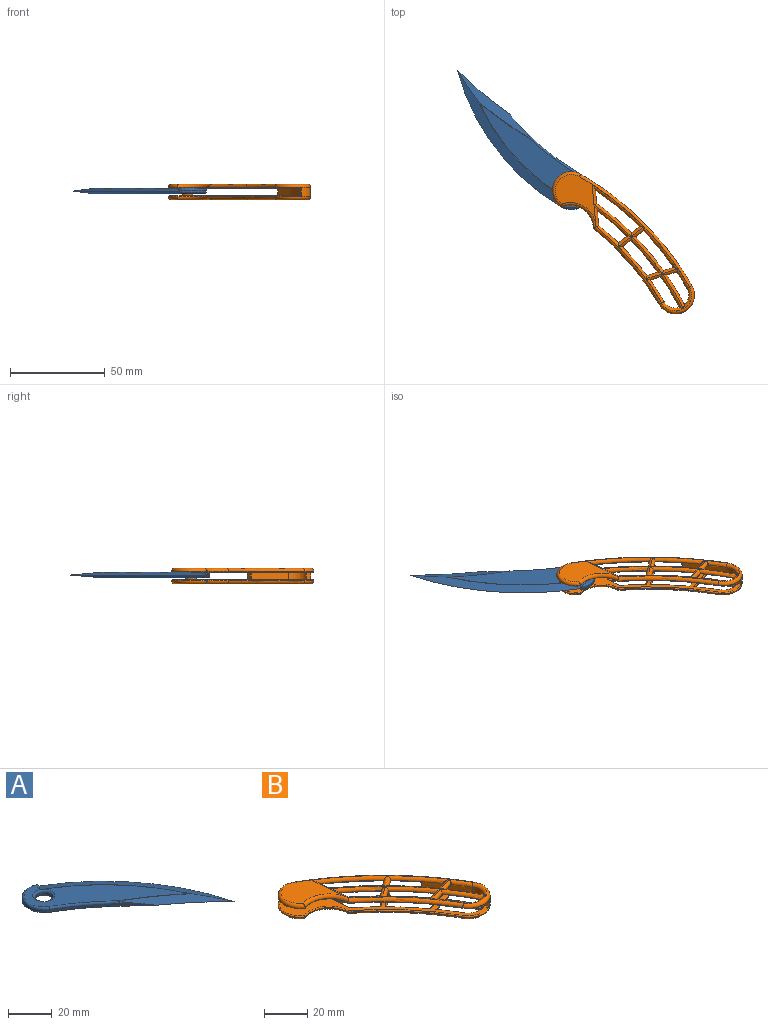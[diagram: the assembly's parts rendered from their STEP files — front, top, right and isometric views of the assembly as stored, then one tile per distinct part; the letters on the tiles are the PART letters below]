
ASSEMBLY  parts=2 mates=1
PART A: 25 faces, bbox 74.4x78.3x3 mm
  f0: cylinder r=140.99mm len=37.78mm, axis (0,0,-1), area 47.3mm2, adj f3,f5,f9,f14,f17
  f1: plane 57.18x54.85mm, normal (0,0,1), area 711.1mm2, adj f15,f17,f19,f20,f21,f24
  f2: plane 57.58x55.37mm, normal (0,0,-1), area 725.8mm2, adj f3,f4,f10,f13,f14,f23
  f3: cone r=205mm half-angle=73.3deg, axis (0,0,-1), area 186.3mm2, adj f0,f2,f4,f5,f14
  f4: cone r=117.87mm half-angle=73.3deg, axis (0,0,1), area 427mm2, adj f2,f3,f6,f8,f9,f10,f11
  f5: cone r=200mm half-angle=73.3deg, axis (0,0,1), area 181.4mm2, adj f0,f3,f6,f17,f19
  f6: cone r=112.87mm half-angle=73.3deg, axis (0,0,-1), area 416.8mm2, adj f4,f5,f7,f9,f16,f20,f21
  f7: plane 0.57x0.33mm, normal (0.87,-0.5,0), area 0.1mm2, adj f6,f16,f20
  f8: plane 0.57x0.33mm, normal (0.87,-0.5,0), area 0.1mm2, adj f4,f10,f11
  f9: cylinder r=10mm len=18.65mm, axis (0,0,-1), area 30.9mm2, adj f0,f4,f6,f11,f13,f15,f16
  f10: cylinder r=0.99mm len=3.92mm, axis (-0.5,-0.87,0), area 4.3mm2, adj f2,f4,f8,f12
  f11: cylinder r=0.99mm len=1.4mm, axis (0,0,-1), area 0.6mm2, adj f4,f8,f9,f12
  f12: sphere r=0.99mm, area 1.6mm2, adj f10,f11,f13
  f13: torus R=9.01mm, axis (0,0,1), area 45.4mm2, adj f2,f9,f12,f14
  f14: torus R=141.98mm, axis (0,0,1), area 55.3mm2, adj f0,f2,f3,f13
  f15: torus R=9.01mm, axis (0,0,1), area 45.4mm2, adj f1,f9,f17,f18
  f16: cylinder r=0.99mm len=1.4mm, axis (0,0,-1), area 0.6mm2, adj f6,f7,f9,f18
  f17: torus R=141.98mm, axis (0,0,1), area 55.4mm2, adj f0,f1,f5,f15,f19
  f18: sphere r=0.99mm, area 1.6mm2, adj f15,f16,f20
  f19: torus R=205.15mm, axis (0,0,1), area 9.6mm2, adj f1,f5,f17,f21
  f20: cylinder r=0.99mm len=4.02mm, axis (0.5,0.87,0), area 4.3mm2, adj f1,f6,f7,f18,f21,f24
  f21: torus R=112.72mm, axis (0,0,1), area 20.2mm2, adj f1,f6,f19,f20,f24
  f22: cylinder r=4mm len=8mm, axis (0,0,1), area 25.1mm2, adj f23,f24
  f23: torus R=5mm, axis (0,0,1), area 43.1mm2, adj f2,f22
  f24: torus R=5mm, axis (0,0,1), area 42.9mm2, adj f1,f20,f21,f22
PART B: 214 faces, bbox 86x86x8.2 mm
  f0: plane 72.02x72.02mm, normal (0,0,1), area 286.6mm2, adj f86,f87,f88,f89,f92,f93,f94,f95
  f1: plane 72.02x72.02mm, normal (0,0,-1), area 286.6mm2, adj f58,f59,f60,f61,f63,f64,f66,f67
  f2: plane 74x68.82mm, normal (0,0,1), area 756mm2, adj f143,f149,f152,f153,f156,f157,f160,f161
  f3: plane 74x68.82mm, normal (0,0,-1), area 756mm2, adj f124,f128,f129,f131,f133,f134,f140,f141
  f4: cylinder r=140.99mm len=40.13mm, axis (0,0,-1), area 0.5mm2, adj f6,f8,f115,f166
  f5: cylinder r=10mm len=18.65mm, axis (0,0,-1), area 0.3mm2, adj f6,f9,f118,f156
  f6: cylinder r=12mm len=16.55mm, axis (0,0,-1), area 0.2mm2, adj f4,f5,f117,f160
  f7: cylinder r=140.99mm len=40.13mm, axis (0,0,-1), area 0.5mm2, adj f8,f11,f120,f155
  f8: cylinder r=10mm len=18.65mm, axis (0,0,-1), area 80mm2, adj f4,f7,f9,f114,f119,f159,f165,f168
  f9: cylinder r=160.99mm len=58.64mm, axis (0,0,-1), area 127.3mm2, adj f5,f8,f10,f116,f121,f137,f141,f142
  f10: cylinder r=10mm len=18.65mm, axis (0,0,-1), area 0.3mm2, adj f9,f11,f123,f147
  f11: cylinder r=12mm len=16.55mm, axis (0,0,-1), area 0.2mm2, adj f7,f10,f122,f151
  f12: cylinder r=157.99mm len=30.39mm, axis (0,0,1), area 116.7mm2, adj f15,f33,f54,f59,f61,f99,f104,f127
  f13: plane 3.2x1.56mm, normal (-0.63,0.78,0), area 6.4mm2, adj f134,f138,f142,f143
  f14: plane 3.2x2.15mm, normal (-0.87,-0.5,0), area 8mm2, adj f15,f158,f168,f174
  f15: cylinder r=7mm len=9.57mm, axis (0,0,1), area 53.4mm2, adj f12,f14,f64,f105,f145,f150,f154,f176
  f16: cylinder r=152.65mm len=18.35mm, axis (0,0,1), area 0.2mm2, adj f17,f19,f110,f210
  f17: plane 6.96x0.64mm, normal (1,0.09,0), area 0.1mm2, adj f16,f18,f112,f209
  f18: cylinder r=157.99mm len=23.29mm, axis (0,0,1), area 0.3mm2, adj f17,f19,f113,f211
  f19: plane 4.3x3.26mm, normal (-0.6,0.8,0), area 0.1mm2, adj f16,f18,f111,f212
  f20: cylinder r=149.65mm len=16.16mm, axis (0,0,1), area 0.2mm2, adj f21,f23,f88,f207
  f21: cylinder r=7mm len=8.18mm, axis (0,0,1), area 0.1mm2, adj f20,f22,f92,f205
  f22: cylinder r=143.99mm len=11.23mm, axis (0,0,1), area 0.1mm2, adj f21,f23,f94,f206
  f23: plane 5.67x1.77mm, normal (0.3,-0.95,0), area 0.1mm2, adj f20,f22,f91,f208
  f24: cylinder r=149.65mm len=16.86mm, axis (0,0,1), area 0.2mm2, adj f25,f27,f87,f203
  f25: plane 5.71x1.78mm, normal (-0.3,0.95,0), area 0.1mm2, adj f24,f26,f90,f201
  f26: cylinder r=143.99mm len=15.19mm, axis (0,0,1), area 0.2mm2, adj f25,f27,f93,f202
  f27: plane 4.54x3.45mm, normal (0.6,-0.8,0), area 0.1mm2, adj f24,f26,f89,f204
  f28: cylinder r=149.65mm len=15.57mm, axis (0,0,1), area 0.2mm2, adj f29,f31,f108,f199
  f29: plane 4.55x3.46mm, normal (-0.6,0.8,0), area 0.1mm2, adj f28,f30,f109,f197
  f30: cylinder r=143.99mm len=10.31mm, axis (0,0,1), area 0.1mm2, adj f29,f31,f107,f198
  f31: plane 7.7x0.71mm, normal (1,0.09,0), area 0.1mm2, adj f28,f30,f106,f200
  f32: cylinder r=152.65mm len=17.74mm, axis (0,0,1), area 0.2mm2, adj f33,f34,f97,f124
  f33: plane 4.29x3.26mm, normal (0.6,-0.8,0), area 0.1mm2, adj f12,f32,f96,f129
  f34: plane 4.71x1.47mm, normal (-0.3,0.95,0), area 0mm2, adj f32,f98,f127,f128
  f35: plane 4.97x1.55mm, normal (0.3,-0.95,0), area 0.1mm2, adj f36,f101,f132,f140
  f36: cylinder r=152.65mm len=14.98mm, axis (0,0,1), area 0.2mm2, adj f35,f103,f145,f146
  f37: plane 4.3x3.26mm, normal (-0.6,0.8,0), area 0.1mm2, adj f38,f40,f85,f196
  f38: cylinder r=157.99mm len=23.29mm, axis (0,0,1), area 0.3mm2, adj f37,f39,f84,f195
  f39: plane 6.96x0.64mm, normal (1,0.09,0), area 0.1mm2, adj f38,f40,f82,f193
  f40: cylinder r=152.65mm len=18.35mm, axis (0,0,1), area 0.2mm2, adj f37,f39,f83,f194
  f41: plane 5.67x1.77mm, normal (0.3,-0.95,0), area 0.1mm2, adj f42,f44,f74,f192
  f42: cylinder r=143.99mm len=11.23mm, axis (0,0,1), area 0.1mm2, adj f41,f43,f73,f190
  f43: cylinder r=7mm len=8.18mm, axis (0,0,1), area 0.1mm2, adj f42,f44,f72,f189
  f44: cylinder r=149.65mm len=16.16mm, axis (0,0,1), area 0.2mm2, adj f41,f43,f75,f191
  f45: plane 4.54x3.45mm, normal (0.6,-0.8,0), area 0.1mm2, adj f46,f48,f81,f188
  f46: cylinder r=143.99mm len=15.19mm, axis (0,0,1), area 0.2mm2, adj f45,f47,f79,f186
  f47: plane 5.71x1.78mm, normal (-0.3,0.95,0), area 0.1mm2, adj f46,f48,f77,f185
  f48: cylinder r=149.65mm len=16.86mm, axis (0,0,1), area 0.2mm2, adj f45,f47,f80,f187
  f49: plane 7.7x0.71mm, normal (1,0.09,0), area 0.1mm2, adj f50,f52,f71,f184
  f50: cylinder r=143.99mm len=10.31mm, axis (0,0,1), area 0.1mm2, adj f49,f51,f69,f182
  f51: plane 4.55x3.46mm, normal (-0.6,0.8,0), area 0.1mm2, adj f50,f52,f68,f181
  f52: cylinder r=149.65mm len=15.57mm, axis (0,0,1), area 0.2mm2, adj f49,f51,f70,f183
  f53: plane 4.71x1.47mm, normal (-0.3,0.95,0), area 0mm2, adj f55,f62,f161,f163
  f54: plane 4.29x3.26mm, normal (0.6,-0.8,0), area 0.1mm2, adj f12,f55,f60,f153
  f55: cylinder r=152.65mm len=17.74mm, axis (0,0,1), area 0.2mm2, adj f53,f54,f63,f157
  f56: cylinder r=152.65mm len=14.98mm, axis (0,0,1), area 0.2mm2, adj f57,f67,f177,f179
  f57: plane 4.97x1.55mm, normal (0.3,-0.95,0), area 0.1mm2, adj f56,f65,f171,f175
  f58: torus R=159.48mm, axis (0,0,1), area 0mm2, adj f1,f59,f61,f162,f164
  f59: torus R=159.48mm, axis (0,0,1), area 60.6mm2, adj f1,f12,f58,f60,f162
  f60: cylinder r=1.49mm len=7.59mm, axis (-0.8,-0.6,0), area 16.1mm2, adj f1,f54,f59,f63
  f61: torus R=159.48mm, axis (0,0,1), area 24.1mm2, adj f1,f12,f58,f64,f164
  f62: cylinder r=1.49mm len=8.62mm, axis (0.95,0.3,0), area 15.4mm2, adj f53,f63,f65,f162
  f63: torus R=151.16mm, axis (0,0,1), area 56.3mm2, adj f1,f55,f60,f62,f66
  f64: torus R=8.49mm, axis (0,0,1), area 25.1mm2, adj f1,f15,f61,f180
  f65: cylinder r=1.49mm len=8.63mm, axis (-0.95,-0.3,0), area 14.7mm2, adj f57,f62,f67,f162,f164
  f66: torus R=151.16mm, axis (0,0,1), area 0mm2, adj f1,f63,f67
  f67: torus R=151.16mm, axis (0,0,1), area 44.7mm2, adj f1,f56,f65,f66,f180
  f68: cylinder r=1.49mm len=7.84mm, axis (0.8,0.6,0), area 16.9mm2, adj f1,f51,f69,f70
  f69: torus R=142.5mm, axis (0,0,1), area 34.4mm2, adj f1,f50,f68,f71
  f70: torus R=151.14mm, axis (0,0,1), area 54.1mm2, adj f1,f52,f68,f71
  f71: cylinder r=1.49mm len=11.75mm, axis (0.09,-1,0), area 22.7mm2, adj f1,f49,f69,f70
  f72: torus R=8.49mm, axis (0,0,1), area 25.8mm2, adj f1,f43,f73,f75
  f73: torus R=142.5mm, axis (0,0,1), area 32.9mm2, adj f1,f42,f72,f74,f76
  f74: cylinder r=1.49mm len=9mm, axis (-0.95,-0.3,0), area 17mm2, adj f41,f73,f75,f77
  f75: torus R=151.14mm, axis (0,0,1), area 46.7mm2, adj f1,f44,f72,f74,f78
  f76: torus R=142.5mm, axis (0,0,1), area 0mm2, adj f1,f73,f79
  f77: cylinder r=1.49mm len=9mm, axis (0.95,0.3,0), area 17.1mm2, adj f47,f74,f79,f80
  f78: torus R=151.14mm, axis (0,0,1), area 0mm2, adj f1,f75,f80
  f79: torus R=142.5mm, axis (0,0,1), area 49mm2, adj f1,f46,f76,f77,f81
  f80: torus R=151.14mm, axis (0,0,1), area 54.7mm2, adj f1,f48,f77,f78,f81
  f81: cylinder r=1.49mm len=7.84mm, axis (-0.8,-0.6,0), area 16.9mm2, adj f1,f45,f79,f80
  f82: cylinder r=1.49mm len=10.87mm, axis (0.09,-1,0), area 20.8mm2, adj f1,f39,f83,f84
  f83: torus R=151.16mm, axis (0,0,1), area 58.4mm2, adj f1,f40,f82,f85
  f84: torus R=159.48mm, axis (0,0,1), area 76.6mm2, adj f1,f38,f82,f85
  f85: cylinder r=1.49mm len=7.59mm, axis (0.8,0.6,0), area 16.1mm2, adj f1,f37,f83,f84
  f86: torus R=151.14mm, axis (0,0,1), area 0mm2, adj f0,f87,f88
  f87: torus R=151.14mm, axis (0,0,1), area 54.7mm2, adj f0,f24,f86,f89,f90
  f88: torus R=151.14mm, axis (0,0,1), area 46.7mm2, adj f0,f20,f86,f91,f92
  f89: cylinder r=1.49mm len=7.84mm, axis (0.8,0.6,0), area 16.9mm2, adj f0,f27,f87,f93
  f90: cylinder r=1.49mm len=9mm, axis (-0.95,-0.3,0), area 17.1mm2, adj f25,f87,f91,f93
  f91: cylinder r=1.49mm len=9mm, axis (0.95,0.3,0), area 17mm2, adj f23,f88,f90,f94
  f92: torus R=8.49mm, axis (0,0,1), area 25.8mm2, adj f0,f21,f88,f94
  f93: torus R=142.5mm, axis (0,0,1), area 49mm2, adj f0,f26,f89,f90,f95
  f94: torus R=142.5mm, axis (0,0,1), area 32.9mm2, adj f0,f22,f91,f92,f95
  f95: torus R=142.5mm, axis (0,0,1), area 0mm2, adj f0,f93,f94
  f96: cylinder r=1.49mm len=7.59mm, axis (0.8,0.6,0), area 16.1mm2, adj f0,f33,f97,f99
  f97: torus R=151.16mm, axis (0,0,1), area 56.3mm2, adj f0,f32,f96,f98,f100
  f98: cylinder r=1.49mm len=8.62mm, axis (-0.95,-0.3,0), area 15.4mm2, adj f34,f97,f101,f125
  f99: torus R=159.48mm, axis (0,0,1), area 60.6mm2, adj f0,f12,f96,f102,f125
  f100: torus R=151.16mm, axis (0,0,1), area 0mm2, adj f0,f97,f103
  f101: cylinder r=1.49mm len=8.63mm, axis (0.95,0.3,0), area 14.7mm2, adj f35,f98,f103,f125,f126
  f102: torus R=159.48mm, axis (0,0,1), area 0mm2, adj f0,f99,f104,f125,f126
  f103: torus R=151.16mm, axis (0,0,1), area 44.7mm2, adj f0,f36,f100,f101,f139
  f104: torus R=159.48mm, axis (0,0,1), area 24.1mm2, adj f0,f12,f102,f105,f126
  f105: torus R=8.49mm, axis (0,0,1), area 25.1mm2, adj f0,f15,f104,f139
  f106: cylinder r=1.49mm len=11.75mm, axis (-0.09,1,0), area 22.7mm2, adj f0,f31,f107,f108
  f107: torus R=142.5mm, axis (0,0,1), area 34.4mm2, adj f0,f30,f106,f109
  f108: torus R=151.14mm, axis (0,0,1), area 54.1mm2, adj f0,f28,f106,f109
  f109: cylinder r=1.49mm len=7.84mm, axis (-0.8,-0.6,0), area 16.9mm2, adj f0,f29,f107,f108
  f110: torus R=151.16mm, axis (0,0,1), area 58.4mm2, adj f0,f16,f111,f112
  f111: cylinder r=1.49mm len=7.59mm, axis (-0.8,-0.6,0), area 16.1mm2, adj f0,f19,f110,f113
  f112: cylinder r=1.49mm len=10.87mm, axis (-0.09,1,0), area 20.8mm2, adj f0,f17,f110,f113
  f113: torus R=159.48mm, axis (0,0,1), area 76.6mm2, adj f0,f18,f111,f112
  f114: torus R=8.51mm, axis (0,0,1), area 69.5mm2, adj f1,f8,f115,f116
  f115: torus R=142.48mm, axis (0,0,1), area 124.7mm2, adj f1,f4,f114,f117
  f116: torus R=159.5mm, axis (0,0,1), area 195.7mm2, adj f1,f9,f114,f118
  f117: torus R=13.49mm, axis (0,0,1), area 56.1mm2, adj f1,f6,f115,f118
  f118: torus R=8.51mm, axis (0,0,1), area 68.7mm2, adj f1,f5,f116,f117
  f119: torus R=8.51mm, axis (0,0,1), area 69.5mm2, adj f0,f8,f120,f121
  f120: torus R=142.48mm, axis (0,0,1), area 124.7mm2, adj f0,f7,f119,f122
  f121: torus R=159.5mm, axis (0,0,1), area 195.7mm2, adj f0,f9,f119,f123
  f122: torus R=13.49mm, axis (0,0,1), area 56.1mm2, adj f0,f11,f120,f123
  f123: torus R=8.51mm, axis (0,0,1), area 68.7mm2, adj f0,f10,f121,f122
  f124: torus R=152.15mm, axis (0,0,1), area 18.5mm2, adj f3,f32,f128,f129
  f125: bspline ~2.99x1.63mm, area 1.7mm2, adj f98,f99,f101,f102,f126,f127
  f126: bspline ~2.04x1.67mm, area 1mm2, adj f101,f102,f104,f125,f132
  f127: cylinder r=0.5mm len=0.76mm, axis (0,0,1), area 0mm2, adj f12,f34,f125,f130
  f128: cylinder r=0.5mm len=5.51mm, axis (0.95,0.3,0), area 4.1mm2, adj f3,f34,f124,f130
  f129: cylinder r=0.5mm len=5.39mm, axis (-0.8,-0.6,0), area 4.6mm2, adj f3,f33,f124,f131
  f130: bspline ~1.24x1.21mm, area 1mm2, adj f12,f127,f128,f133
  f131: torus R=158.49mm, axis (0,0,1), area 10.8mm2, adj f3,f12,f129,f135
  f132: cylinder r=0.5mm len=0.57mm, axis (0,0,1), area 0mm2, adj f12,f35,f126,f136
  f133: torus R=157.49mm, axis (0,0,1), area 1.5mm2, adj f3,f12,f130,f136
  f134: cylinder r=0.5mm len=1.87mm, axis (-0.78,-0.63,0), area 1.6mm2, adj f3,f13,f135,f137
  f135: bspline ~1.18x1.17mm, area 0.8mm2, adj f12,f131,f134,f138
  f136: bspline ~1.22x1.06mm, area 0.8mm2, adj f12,f132,f133,f140
  f137: bspline ~1.22x1.07mm, area 0.8mm2, adj f9,f134,f141,f142
  f138: cylinder r=0.5mm len=3.2mm, axis (0,0,1), area 2.5mm2, adj f12,f13,f135,f144
  f139: bspline ~2.83x1.64mm, area 1.1mm2, adj f103,f105,f145
  f140: cylinder r=0.5mm len=5.77mm, axis (-0.95,-0.3,0), area 4.2mm2, adj f3,f35,f136,f146
  f141: torus R=160.49mm, axis (0,0,1), area 46.1mm2, adj f3,f9,f137,f147
  f142: cylinder r=0.5mm len=3.2mm, axis (0,0,-1), area 2.5mm2, adj f9,f13,f137,f148
  f143: cylinder r=0.5mm len=1.87mm, axis (0.78,0.63,0), area 1.6mm2, adj f2,f13,f144,f148
  f144: bspline ~1.22x1.16mm, area 0.8mm2, adj f12,f138,f143,f149
  f145: cylinder r=0.5mm len=0.82mm, axis (0,0,1), area 0mm2, adj f15,f36,f139,f150
  f146: torus R=152.15mm, axis (0,0,1), area 14.1mm2, adj f3,f36,f140,f150
  f147: torus R=9.5mm, axis (0,0,1), area 24.1mm2, adj f3,f10,f141,f151
  f148: bspline ~1.17x1.09mm, area 0.8mm2, adj f9,f142,f143,f152
  f149: torus R=158.49mm, axis (0,0,1), area 10.8mm2, adj f2,f12,f144,f153
  f150: bspline ~1.21x1.19mm, area 1mm2, adj f15,f145,f146,f154
  f151: torus R=12.5mm, axis (0,0,1), area 18.7mm2, adj f3,f11,f147,f155
  f152: torus R=160.49mm, axis (0,0,1), area 46.1mm2, adj f2,f9,f148,f156
  f153: cylinder r=0.5mm len=5.39mm, axis (0.8,0.6,0), area 4.6mm2, adj f2,f54,f149,f157
  f154: torus R=6.5mm, axis (0,0,1), area 1mm2, adj f3,f15,f150,f158
  f155: torus R=141.49mm, axis (0,0,1), area 41.9mm2, adj f3,f7,f151,f159
  f156: torus R=9.5mm, axis (0,0,1), area 24.1mm2, adj f2,f5,f152,f160
  f157: torus R=152.15mm, axis (0,0,1), area 18.5mm2, adj f2,f55,f153,f161
  f158: cylinder r=0.5mm len=2.85mm, axis (0.5,-0.87,0), area 2.2mm2, adj f3,f14,f154,f165
  f159: torus R=9.5mm, axis (0,0,1), area 11.7mm2, adj f3,f8,f155,f165
  f160: torus R=12.5mm, axis (0,0,1), area 18.7mm2, adj f2,f6,f156,f166
  f161: cylinder r=0.5mm len=5.51mm, axis (-0.95,-0.3,0), area 4.1mm2, adj f2,f53,f157,f167
  f162: bspline ~2.99x1.63mm, area 1.7mm2, adj f58,f59,f62,f65,f163,f164
  f163: cylinder r=0.5mm len=0.76mm, axis (0,0,1), area 0mm2, adj f12,f53,f162,f167
  f164: bspline ~2.04x1.67mm, area 1mm2, adj f58,f61,f65,f162,f171
  f165: bspline ~1.24x1.17mm, area 0.9mm2, adj f8,f158,f159,f168
  f166: torus R=141.49mm, axis (0,0,1), area 41.9mm2, adj f2,f4,f160,f169
  f167: bspline ~1.21x1.2mm, area 1mm2, adj f12,f161,f163,f170
  f168: cylinder r=0.5mm len=3.2mm, axis (0,0,-1), area 2.6mm2, adj f8,f14,f165,f172
  f169: torus R=9.5mm, axis (0,0,1), area 11.7mm2, adj f2,f8,f166,f172
  f170: torus R=157.49mm, axis (0,0,1), area 1.5mm2, adj f2,f12,f167,f173
  f171: cylinder r=0.5mm len=0.57mm, axis (0,0,1), area 0mm2, adj f12,f57,f164,f173
  f172: bspline ~1.22x1.22mm, area 0.9mm2, adj f8,f168,f169,f174
  f173: bspline ~1.2x1.1mm, area 0.8mm2, adj f12,f170,f171,f175
  f174: cylinder r=0.5mm len=2.85mm, axis (-0.5,0.87,0), area 2.2mm2, adj f2,f14,f172,f176
  f175: cylinder r=0.5mm len=5.77mm, axis (0.95,0.3,0), area 4.2mm2, adj f2,f57,f173,f177
  f176: torus R=6.5mm, axis (0,0,1), area 1mm2, adj f2,f15,f174,f178
  f177: torus R=152.15mm, axis (0,0,1), area 14.1mm2, adj f2,f56,f175,f178
  f178: bspline ~1.21x1.18mm, area 1mm2, adj f15,f176,f177,f179
  f179: cylinder r=0.5mm len=0.82mm, axis (0,0,1), area 0mm2, adj f15,f56,f178,f180
  f180: bspline ~2.83x1.64mm, area 1.1mm2, adj f64,f67,f179
  f181: cylinder r=0.5mm len=5.66mm, axis (-0.8,-0.6,0), area 4.9mm2, adj f2,f51,f182,f183
  f182: torus R=143.49mm, axis (0,0,1), area 11.1mm2, adj f2,f50,f181,f184
  f183: torus R=150.15mm, axis (0,0,1), area 16.8mm2, adj f2,f52,f181,f184
  f184: cylinder r=0.5mm len=9.07mm, axis (-0.09,1,0), area 6.6mm2, adj f2,f49,f182,f183
  f185: cylinder r=0.5mm len=6.86mm, axis (-0.95,-0.3,0), area 5.1mm2, adj f2,f47,f186,f187
  f186: torus R=143.49mm, axis (0,0,1), area 16.1mm2, adj f2,f46,f185,f188
  f187: torus R=150.15mm, axis (0,0,1), area 17.8mm2, adj f2,f48,f185,f188
  f188: cylinder r=0.5mm len=5.65mm, axis (0.8,0.6,0), area 4.9mm2, adj f2,f45,f186,f187
  f189: torus R=7.5mm, axis (0,0,1), area 7.9mm2, adj f2,f43,f190,f191
  f190: torus R=143.49mm, axis (0,0,1), area 10.7mm2, adj f2,f42,f189,f192
  f191: torus R=150.15mm, axis (0,0,1), area 15.2mm2, adj f2,f44,f189,f192
  f192: cylinder r=0.5mm len=6.83mm, axis (0.95,0.3,0), area 5.1mm2, adj f2,f41,f190,f191
  f193: cylinder r=0.5mm len=8.28mm, axis (-0.09,1,0), area 6mm2, adj f2,f39,f194,f195
  f194: torus R=152.15mm, axis (0,0,1), area 19.1mm2, adj f2,f40,f193,f196
  f195: torus R=158.49mm, axis (0,0,1), area 24.4mm2, adj f2,f38,f193,f196
  f196: cylinder r=0.5mm len=5.4mm, axis (-0.8,-0.6,0), area 4.6mm2, adj f2,f37,f194,f195
  f197: cylinder r=0.5mm len=5.66mm, axis (0.8,0.6,0), area 4.9mm2, adj f3,f29,f198,f199
  f198: torus R=143.49mm, axis (0,0,1), area 11.1mm2, adj f3,f30,f197,f200
  f199: torus R=150.15mm, axis (0,0,1), area 16.8mm2, adj f3,f28,f197,f200
  f200: cylinder r=0.5mm len=9.07mm, axis (0.09,-1,0), area 6.6mm2, adj f3,f31,f198,f199
  f201: cylinder r=0.5mm len=6.86mm, axis (0.95,0.3,0), area 5.1mm2, adj f3,f25,f202,f203
  f202: torus R=143.49mm, axis (0,0,1), area 16.1mm2, adj f3,f26,f201,f204
  f203: torus R=150.15mm, axis (0,0,1), area 17.8mm2, adj f3,f24,f201,f204
  f204: cylinder r=0.5mm len=5.65mm, axis (-0.8,-0.6,0), area 4.9mm2, adj f3,f27,f202,f203
  f205: torus R=7.5mm, axis (0,0,1), area 7.9mm2, adj f3,f21,f206,f207
  f206: torus R=143.49mm, axis (0,0,1), area 10.7mm2, adj f3,f22,f205,f208
  f207: torus R=150.15mm, axis (0,0,1), area 15.2mm2, adj f3,f20,f205,f208
  f208: cylinder r=0.5mm len=6.83mm, axis (-0.95,-0.3,0), area 5.1mm2, adj f3,f23,f206,f207
  f209: cylinder r=0.5mm len=8.28mm, axis (0.09,-1,0), area 6mm2, adj f3,f17,f210,f211
  f210: torus R=152.15mm, axis (0,0,1), area 19.1mm2, adj f3,f16,f209,f212
  f211: torus R=158.49mm, axis (0,0,1), area 24.4mm2, adj f3,f18,f209,f212
  f212: cylinder r=0.5mm len=5.4mm, axis (0.8,0.6,0), area 4.6mm2, adj f3,f19,f210,f211
  f213: cylinder r=3mm len=6mm, axis (0,0,-1), area 79.2mm2, adj f2,f3
PLACE A rot(axis=(0,0,-1),180deg) t=(-42.37,30.36,2.18)mm
PLACE B t=(12.63,-24.64,1.68)mm
MATE revolute A.f9 <-> B.f5  axis (0,0,1) through (-14.87,2.86,1.68)mm
